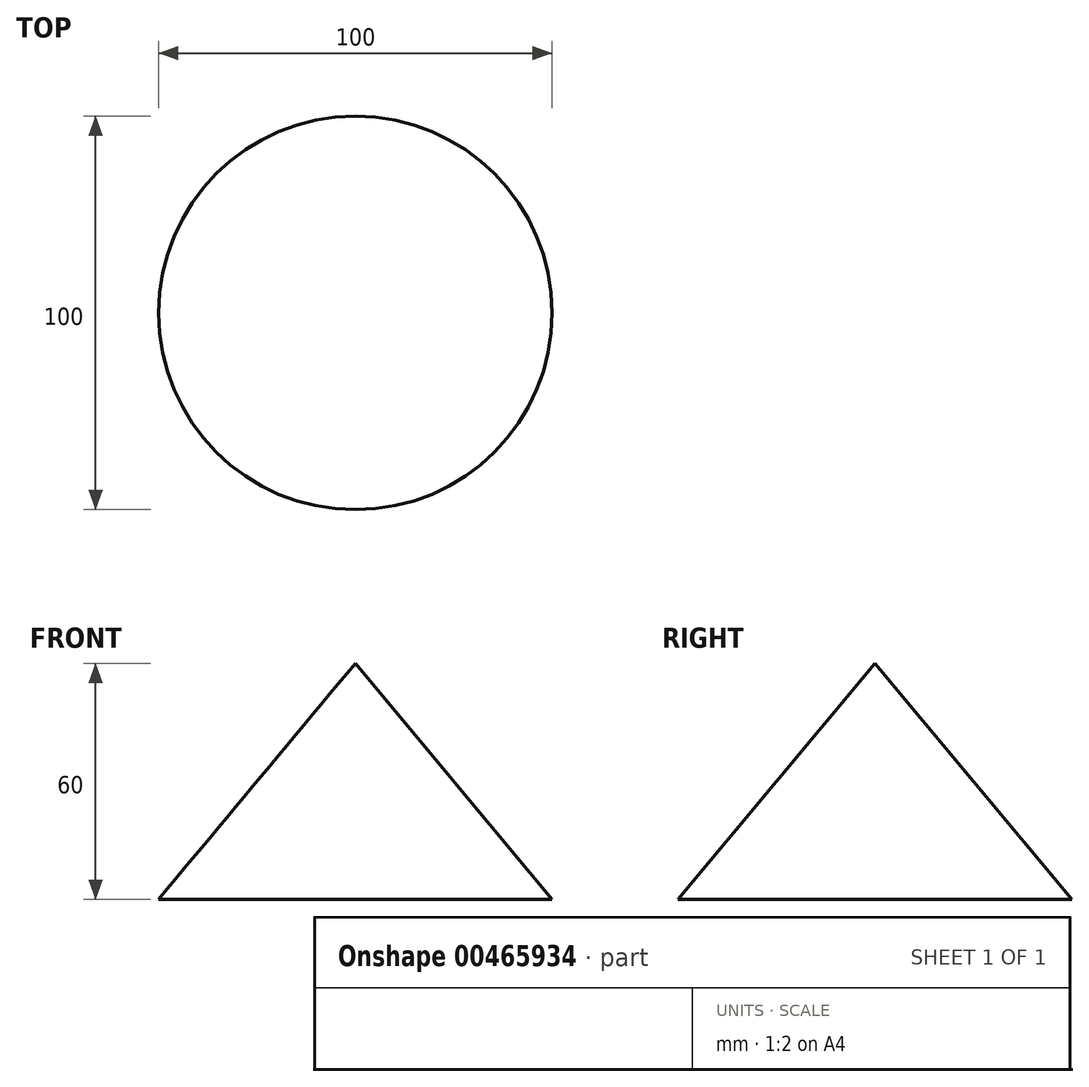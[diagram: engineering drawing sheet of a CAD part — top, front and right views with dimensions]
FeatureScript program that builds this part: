
annotation { "Feature Type Name" : "Feature", "Feature Type Description" : "" }
export const myFeature = defineFeature(function(context is Context, id is Id, definition is map)
    precondition{}
    {
        {
            var Q0;
            Q0=qCreatedBy(makeId("Front.planeOp"),FACE);
            var sketch = newSketch(context, id + "F0", { "sketchPlane" : qUnion([Q0])});
            skLineSegment(sketch, "E0", {"start": v(0, 0) * mm, "end": v(0, 60) * mm});
            skLineSegment(sketch, "E1", {"start": v(0, 60) * mm, "end": v(0, 60) * mm});
            skLineSegment(sketch, "E2", {"start": v(50, 0) * mm, "end": v(0, 60) * mm});
            skLineSegment(sketch, "E3", {"start": v(50, 0) * mm, "end": v(0, 0) * mm});
            skSolve(sketch);
        }
        {
            var Q0;
            Q0=makeQuery(id+"F0.imprint","IMPRINT",FACE,{"disambiguationData":[TD([[makeQuery(id+"F0.imprint","IMPRINT",EDGE,{"derivedFrom":sQuery(id+"F0.wireOp",EDGE,"E0")}),-1.0]])]});
            var Q1;
            Q1=sQuery(id+"F0.wireOp",EDGE,"E0");
            revolve(context, id + "F1", {"entities" : qUnion([Q0]), "axis" : qUnion([Q1]), "revolveType" : RevolveType.FULL});
        }
    });
